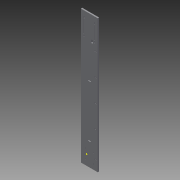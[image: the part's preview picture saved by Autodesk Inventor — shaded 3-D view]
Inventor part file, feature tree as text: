
AUTODESK INVENTOR PART (.ipt)
format: ipt  version: 2015 (Build 190159000, 159)  size: 173,056 bytes
history: native  units: in
note: dims shown in document units (in); Inventor stores cm internally (conversion verified against a paired STEP export)
features: sketch x2, extrude x1
ambient origin geometry x8: Origin, YZ Plane, XZ Plane, XY Plane, X Axis, Y Axis, Z Axis, Center Point
bodies: Body1 (feature_tree)
feature tree (3):
  sketch  "Sketch1"  dims[d0=3.0in d4=0.075in]
  extrude  "Extrusion3"  Depth=0.075in
  sketch  "Sketch2"  dims[d5=0.3125in d8=2.3in d13=0.3125in d16=0.25in d17=0.14in d18=0.5in d59=0.236in d60=0.0in]
